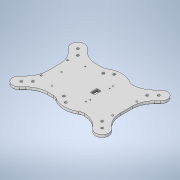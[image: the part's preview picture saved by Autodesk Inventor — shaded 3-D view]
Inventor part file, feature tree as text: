
AUTODESK INVENTOR PART (.ipt)
format: ipt  version: 2020.3 (Build 243373000, 373)  size: 422,912 bytes
history: native  units: mm
features: hole x3, fillet x2, sketch x1, extrude x1
ambient origin geometry x8: Origin, YZ Plane, XZ Plane, XY Plane, X Axis, Y Axis, Z Axis, Center Point
bodies: Body1 (feature_tree)
feature tree (7):
  sketch  "Sketch1"  dims[d0=135.0deg d4=24.6mm d5=12.4mm d9=8.7mm d10=135.0deg d12=6.0mm d13=2.0mm d14=2.0mm d16=20.0mm d23=6.0mm d29=135.0mm d32=15.0mm d33=4.0mm d34=28.4mm d38=4.0mm d40=6.8mm d60=90.0mm d61=135.0deg d70=135.0deg d102=5.0mm d103=0.0mm d104=4.2mm d105=6.0mm d106=8.3mm d107=2.0mm d108=90.0deg d109=8.8mm d110=0.0mm d111=40.0mm d113=22.0mm d114=35.0mm d115=25.0mm d116=31.0mm d117=35.3mm d118=36.0mm d119=18.0mm d120=17.5mm d121=10.0mm d122=20.0mm d123=93.0mm d124=91.7mm d125=1.9mm d126=6.0mm d127=4.0mm d128=2.0mm d129=90.0deg d130=8.0mm d131=0.0mm d153=0.5mm d154=12.0mm d157=6.0mm d158=2.094395mm d159=6.0mm d160=3.8mm d161=2.0mm d162=2.0mm d163=2.0mm d164=2.0mm d165=6.0mm d166=12.0mm d167=5.0mm d168=1.0mm d169=3.0mm d170=45.0mm d171=3.0mm d172=6.0mm d173=6.3mm d174=2.0mm d175=90.0deg d176=8.0mm d177=20.594885mm d178=30.0deg d179=25.0mm d180=10.0mm d182=4.0mm d183=15.0mm]
  extrude  "Extrusion12"  Depth=15.0mm
  hole  "Hole2"  [1 undecoded]
  fillet  "Fillet10"  Radius=8.7mm
  hole  "Hole3"  [1 undecoded]
  fillet  "Fillet15"  Radius=6.0mm
  hole  "Hole4"  [1 undecoded]
note: 3 required parameter values undecoded (feature->parameter linkage not recoverable at this tier; creation-order binding heuristic only, values carry confidence <= 0.55)
